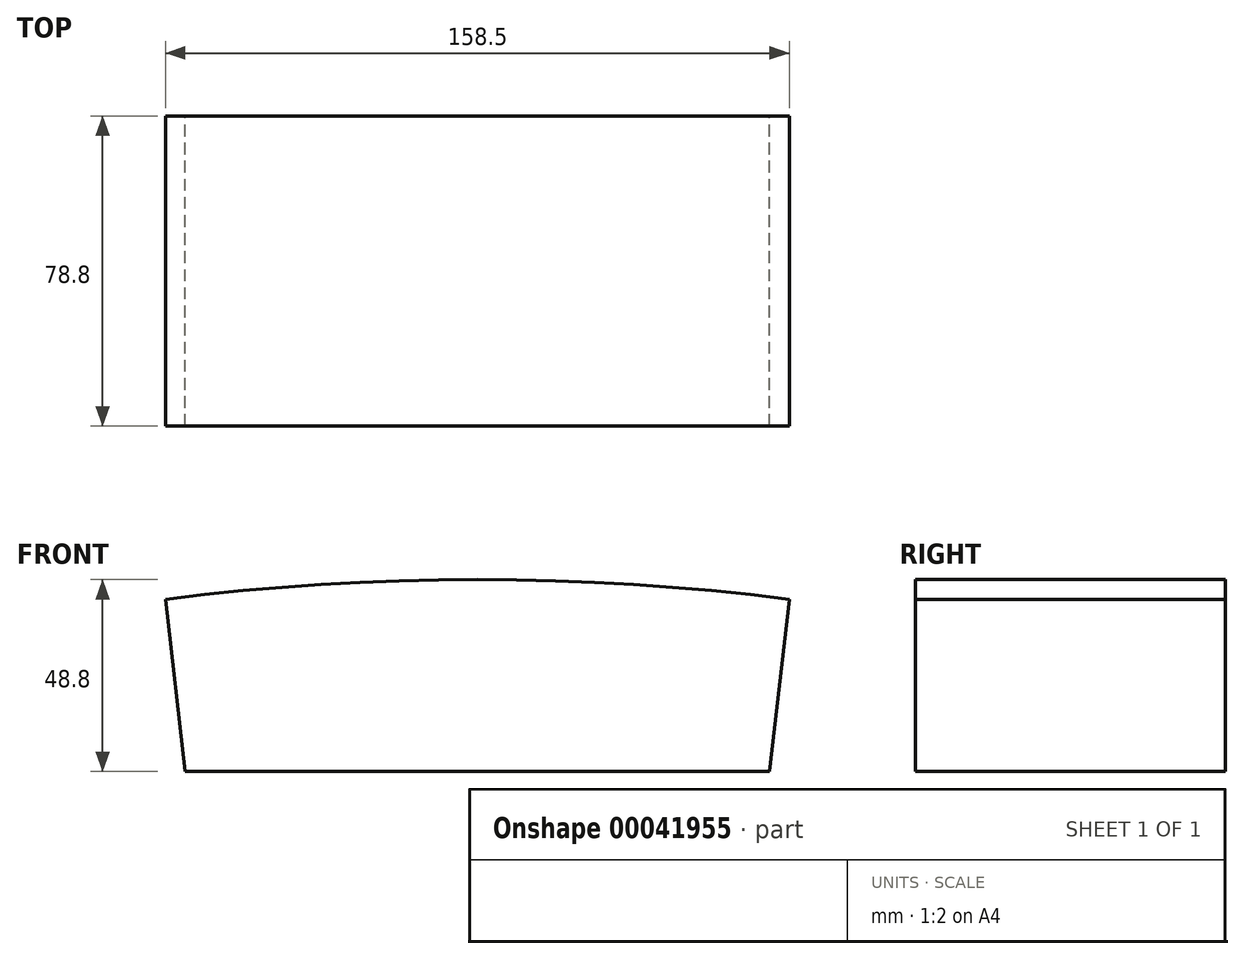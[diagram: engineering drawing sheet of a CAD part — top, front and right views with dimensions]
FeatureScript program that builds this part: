
annotation { "Feature Type Name" : "Feature", "Feature Type Description" : "" }
export const myFeature = defineFeature(function(context is Context, id is Id, definition is map)
    precondition{}
    {
        {
            var Q0;
            Q0=qCreatedBy(makeId("Front.planeOp"),FACE);
            var sketch = newSketch(context, id + "F0", { "sketchPlane" : qUnion([Q0])});
            skLineSegment(sketch, "E0.bottom", {"start": v(-62.92, -37.3) * mm, "end": v(95.58, -37.3) * mm});
            skLineSegment(sketch, "E0.left", {"start": v(-62.92, -37.3) * mm, "end": v(-62.92, 11.5) * mm});
            skLineSegment(sketch, "E0.right", {"start": v(95.58, -37.3) * mm, "end": v(95.58, 11.5) * mm});
            skLineSegment(sketch, "E1", {"start": v(-71.8, 6.5) * mm, "end": v(-62.92, 6.5) * mm});
            skLineSegment(sketch, "E2", {"start": v(-62.92, 6.5) * mm, "end": v(-57.92, -37.3) * mm});
            skLineSegment(sketch, "E3", {"start": v(95.58, 6.5) * mm, "end": v(90.58, -37.3) * mm});
            skLineSegment(sketch, "E4", {"start": v(16.33, 11.5) * mm, "end": v(16.33, 27.45) * mm});
            skArc(sketch, "E5", {"start": v(95.58, 6.5) * mm, "mid": v(16.33, 11.5) * mm, "end": v(-62.92, 6.5) * mm});
            skLineSegment(sketch, "E6.trimOffspring", {"start": v(95.58, 6.5) * mm, "end": v(104.16, 6.5) * mm});
            skSolve(sketch);
        }
        {
            var Q0;
            {var subQ2=sQuery(id+"F0.wireOp",EDGE,"E2");Q0=makeQuery(id+"F0.imprint","IMPRINT",FACE,{"disambiguationData":[TD([[makeQuery(id+"F0.imprint","IMPRINT",EDGE,{"derivedFrom":subQ2}),1.0]])]});}
            extrude(context, id + "F1", {"entities" : qUnion([Q0]), "depth" : 78.8 * mm});
        }
    });
